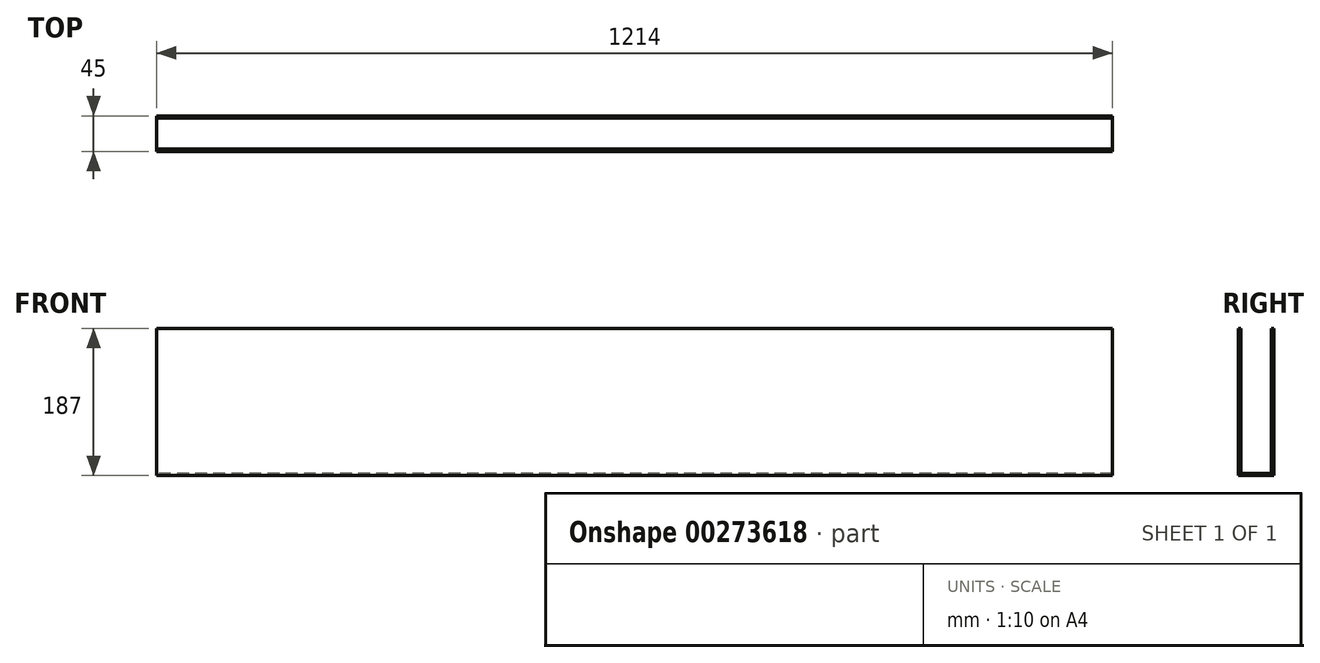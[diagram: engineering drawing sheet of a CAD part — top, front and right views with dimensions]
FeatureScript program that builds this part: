
annotation { "Feature Type Name" : "Feature", "Feature Type Description" : "" }
export const myFeature = defineFeature(function(context is Context, id is Id, definition is map)
    precondition{}
    {
        {
            var Q0;
            Q0=qCreatedBy(makeId("Right.planeOp"),FACE);
            var sketch = newSketch(context, id + "F0", { "sketchPlane" : qUnion([Q0])});
            skLineSegment(sketch, "E0", {"start": v(0, 0) * mm, "end": v(0, 187) * mm});
            skLineSegment(sketch, "E1", {"start": v(0, 0) * mm, "end": v(45, 0) * mm});
            skLineSegment(sketch, "E2", {"start": v(45, 187) * mm, "end": v(45, 0) * mm});
            skLineSegment(sketch, "E3.0", {"start": v(42, 187) * mm, "end": v(42, 3) * mm});
            skLineSegment(sketch, "E3.1", {"start": v(3, 3) * mm, "end": v(42, 3) * mm});
            skLineSegment(sketch, "E3.2", {"start": v(3, 3) * mm, "end": v(3, 187) * mm});
            skLineSegment(sketch, "E4", {"start": v(0, 187) * mm, "end": v(3, 187) * mm});
            skLineSegment(sketch, "E5", {"start": v(42, 187) * mm, "end": v(45, 187) * mm});
            skSolve(sketch);
        }
        {
            var Q0;
            Q0 = qSketchRegion(id + "F0", true);
            extrude(context, id + "F1", {"entities" : qUnion([Q0]), "depth" : 1214 * mm});
        }
    });
